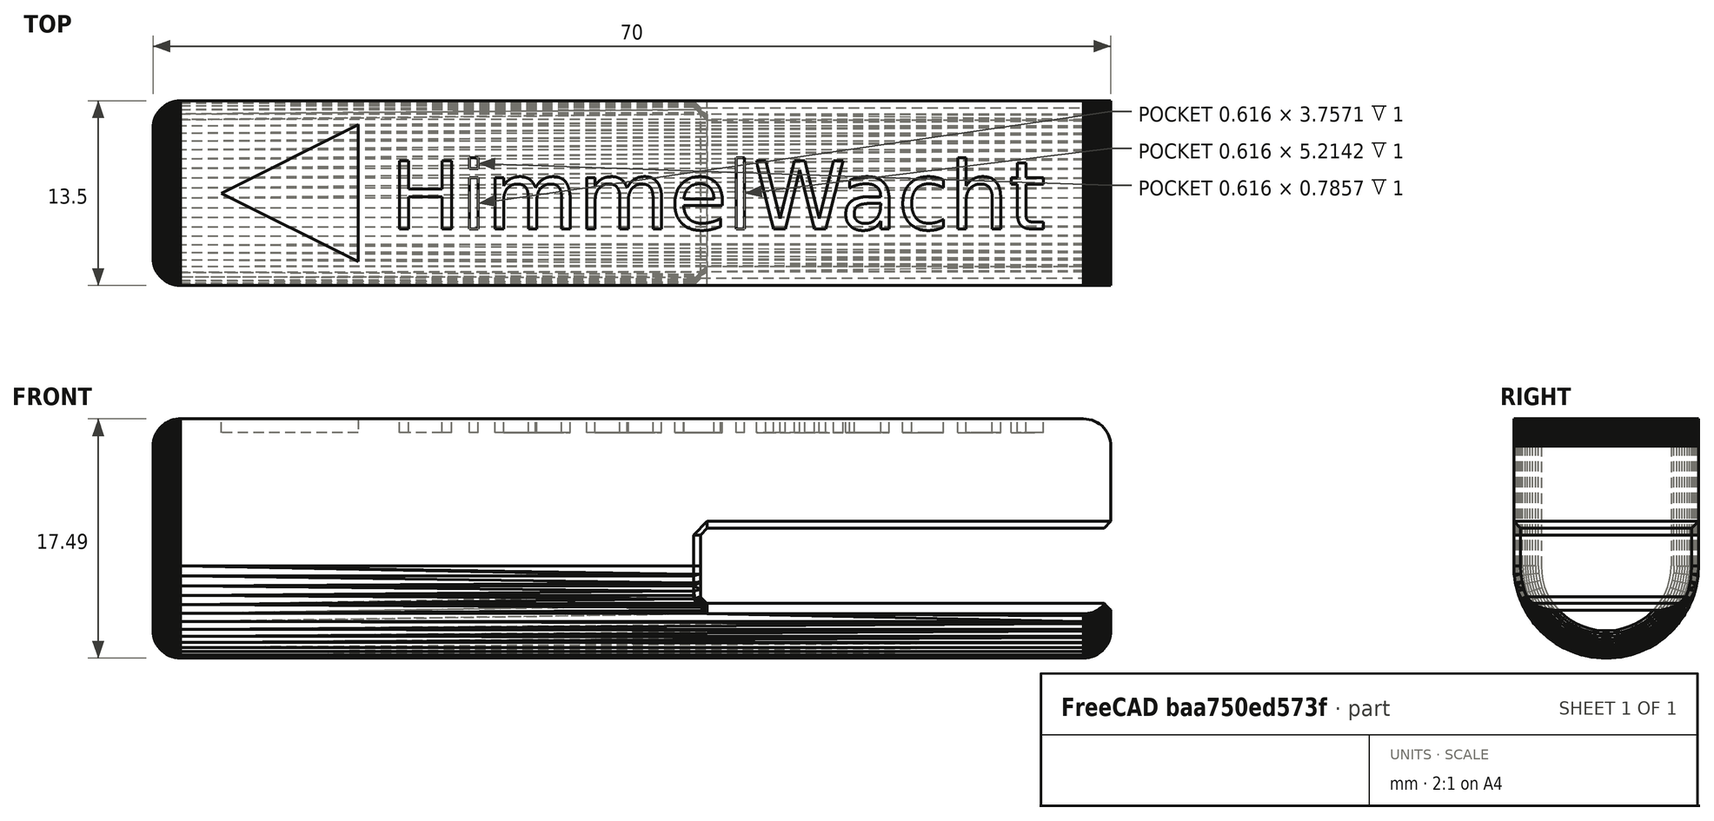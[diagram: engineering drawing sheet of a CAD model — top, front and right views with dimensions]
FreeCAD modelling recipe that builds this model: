
FCSTD DOCUMENT  (FreeCAD 1.0R39109 (Git))
Label: weight
License: All rights reserved
LicenseURL: https://en.wikipedia.org/wiki/All_rights_reserved
objects: Sketcher::SketchObject×2, Part::Extrusion×2, Part::Feature×1, Part::Fuse×1, Part::Part2DObjectPython×1, Part::Cut×1, Mesh::Feature×1
note: 10 computed .brp shape members not serialized (recipe doc carries the construction recipe); baked Part::Feature solids carry a one-line shape summary decoded from their .brp

FEATURE [Part::Feature] Weight_V004_solid  label="Weight_V004 (Solid)"
  shape: bbox 70 x 13.5 x 17.49 mm, 1790 faces (baked)
FEATURE [Sketcher::SketchObject] Sketch
  ArcFitTolerance = 1e-06
  AttachmentSupport = -> [Weight_V004_solid]
  ExternalGeometry = -> [Weight_V004_solid]
  FullyConstrained = true
  MakeInternals = false
  MapMode = 5
  Placement = pos=(0,0,10.75) rot=(0,0,1;0rad)
  sketch-geometry (4):
    g0: LineSegment StartX=-55 StartY=2 StartZ=0 EndX=-55 EndY=-2 EndZ=0
    g1: LineSegment StartX=-55 StartY=-2 StartZ=0 EndX=-15 EndY=-2 EndZ=0
    g2: LineSegment StartX=-15 StartY=-2 StartZ=0 EndX=-15 EndY=2 EndZ=0
    g3: LineSegment StartX=-15 StartY=2 StartZ=0 EndX=-55 EndY=2 EndZ=0
  constraints (10):
    c: Coincident(g0,g1)
    c: Coincident(g1,g2)
    c: Coincident(g2,g3)
    c: Coincident(g3,g0)
    c: Vertical(g0)
    c: Vertical(g2)
    c: Horizontal(g1)
    c: Horizontal(g3)
    c: Coincident(g0,g-3)
    c: Coincident(g1,g-5)
FEATURE [Part::Extrusion] Extrude001
  Base = -> Sketch
  Dir = (0,0,1)
  DirMode = 2
  FaceMakerClass = Part::FaceMakerBullseye
  FaceMakerMode = 3
  LengthFwd = -1
  LengthRev = 0
  Solid = true
  Symmetric = false
FEATURE [Part::Fuse] Fusion  label="weight"
  Base = -> Weight_V004_solid
  Tool = -> Extrude001
FEATURE [Sketcher::SketchObject] Sketch001  label="placement-helper"
  ArcFitTolerance = 1e-06
  AttachmentSupport = -> [Fusion]
  ExternalGeometry = -> [Fusion]
  FullyConstrained = true
  MakeInternals = false
  MapMode = 5
  Placement = pos=(0,0,10.75) rot=(0,0,1;0rad)
  sketch-geometry (4):
    g0: LineSegment StartX=-52 StartY=5 StartZ=0 EndX=-52 EndY=-5 EndZ=0
    g1: LineSegment StartX=-52 StartY=-5 StartZ=0 EndX=-5 EndY=-5 EndZ=0
    g2: LineSegment StartX=-5 StartY=-5 StartZ=0 EndX=-5 EndY=5 EndZ=0
    g3: LineSegment StartX=-5 StartY=5 StartZ=0 EndX=-52 EndY=5 EndZ=0
  constraints (12):
    c: Coincident(g0,g1)
    c: Coincident(g1,g2)
    c: Coincident(g2,g3)
    c: Coincident(g3,g0)
    c: Vertical(g0)
    c: Vertical(g2)
    c: Horizontal(g1)
    c: Horizontal(g3)
    c: Distance(g0,g-4) = 1.75
    c: Distance(g0,g-5) = 1.75
    c: Distance(g-3,g2) = 3
    c: Distance(g-8,g0) = 3
FEATURE [Part::Part2DObjectPython] ShapeString  label="HimmelWacht"  # Draft 2D object (typed FeaturePython)
  FontFile = <path>
  Fuse = false
  Justification = 6
  JustificationReference = 0
  KeepLeftMargin = false
  MakeFace = true
  ObliqueAngle = 0
  Placement = pos=(-52.0293,-2.38234,9) rot=(0,0,1;0rad)
  ScaleToSize = true
  Size = 5
  String = HimmelWacht
  Tracking = 0
FEATURE [Part::Extrusion] Extrude  label="3D-Text"
  Base = -> ShapeString
  Dir = (0,0,1)
  DirMode = 2
  FaceMakerClass = Part::FaceMakerBullseye
  FaceMakerMode = 3
  LengthFwd = 1
  LengthRev = 0
  Placement = pos=(0.02929,-0.25,0.75) rot=(0,0,1;0rad)
  Solid = false
  Symmetric = false
FEATURE [Part::Cut] Cut  label="weight-with-text"
  Base = -> Fusion
  Tool = -> Extrude
FEATURE [Mesh::Feature] Mesh  label="weight-with-text (Meshed)"
note: 1 file-system path scrubbed to <path> (originals preserved in the JSON sidecar)
